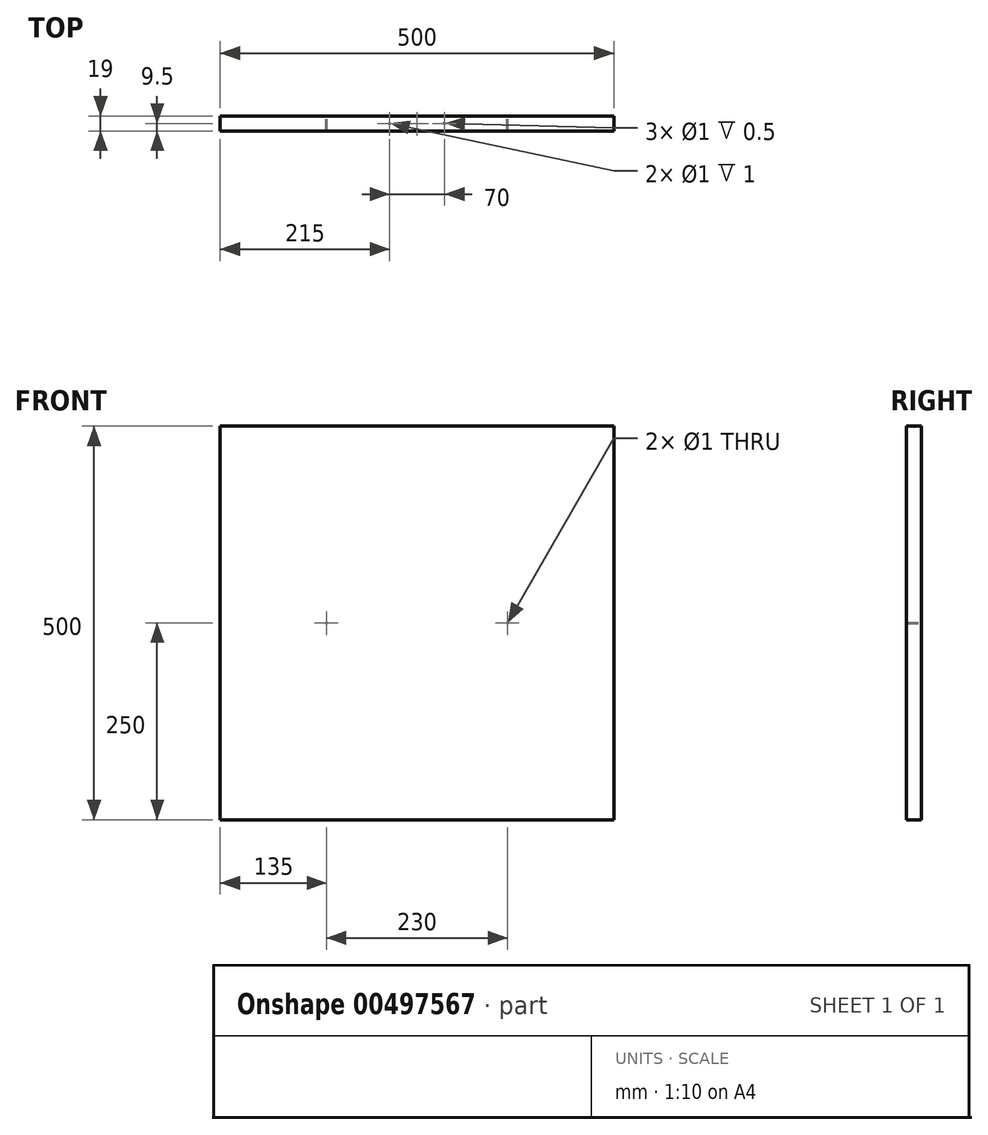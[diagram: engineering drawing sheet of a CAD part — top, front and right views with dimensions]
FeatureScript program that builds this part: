
annotation { "Feature Type Name" : "Feature", "Feature Type Description" : "" }
export const myFeature = defineFeature(function(context is Context, id is Id, definition is map)
    precondition{}
    {
        {
            var Q0;
            Q0=qCreatedBy(makeId("Front.planeOp"),FACE);
            var sketch = newSketch(context, id + "F0", { "sketchPlane" : qUnion([Q0])});
            skLineSegment(sketch, "E0.bottom", {"start": v(0, 500) * mm, "end": v(500, 500) * mm});
            skLineSegment(sketch, "E0.top", {"start": v(0, 0) * mm, "end": v(500, 0) * mm});
            skLineSegment(sketch, "E0.left", {"start": v(0, 500) * mm, "end": v(0, 0) * mm});
            skLineSegment(sketch, "E0.right", {"start": v(500, 500) * mm, "end": v(500, 0) * mm});
            skCircle(sketch, "E1", {"center": v(135, 250) * mm, "radius": 0.5 * mm});
            skLineSegment(sketch, "E2", {"start": v(250, 500) * mm, "end": v(250, 0) * mm, "construction": true});
            skCircle(sketch, "E3.MirrorC", {"center": v(365, 250) * mm, "radius": 0.5 * mm});
            skSolve(sketch);
        }
        {
            var Q0;
            Q0=makeQuery(id+"F0.imprint","IMPRINT",FACE,{"disambiguationData":[TD([[makeQuery(id+"F0.imprint","IMPRINT",EDGE,{"derivedFrom":sQuery(id+"F0.wireOp",EDGE,"E0.bottom")}),-1.0]])]});
            extrude(context, id + "F1", {"entities" : qUnion([Q0]), "depth" : 19 * mm});
        }
        {
            var Q0;
            Q0=makeQuery(id+"F1.opExtrude","SWEPT_FACE",FACE,{"disambiguationData":[OSD([sQuery(id+"F0.wireOp",EDGE,"E0.top")])]});
            var sketch = newSketch(context, id + "F2", { "sketchPlane" : qUnion([Q0])});
            skCircle(sketch, "E4", {"center": v(250, 9.5) * mm, "radius": 0.5 * mm});
            skPoint(sketch, "E4.centerSnap0", {"position": v(250, 0) * mm});
            skPoint(sketch, "E4.centerSnap1", {"position": v(0, 9.5) * mm});
            skLineSegment(sketch, "E5", {"start": v(250, 0) * mm, "end": v(250, 19) * mm, "construction": true});
            skCircle(sketch, "E6", {"center": v(215, 9.5) * mm, "radius": 0.5 * mm});
            skCircle(sketch, "E7.MirrorC", {"center": v(285, 9.5) * mm, "radius": 0.5 * mm});
            skSolve(sketch);
        }
        {
            var Q0;
            Q0 = qSketchRegion(id + "F2", true);
            extrude(context, id + "F3", {"entities" : qUnion([Q0]), "operationType" : NewBodyOperationType.REMOVE, "oppositeDirection" : true, "depth" : 1 * mm, "symmetric" : true});
        }
        {
            var Q0;
            Q0=makeQuery(id+"F1.opExtrude","SWEPT_FACE",FACE,{"disambiguationData":[OSD([sQuery(id+"F0.wireOp",EDGE,"E0.bottom")])]});
            var sketch = newSketch(context, id + "F4", { "sketchPlane" : qUnion([Q0])});
            skLineSegment(sketch, "E8", {"start": v(250, 0) * mm, "end": v(250, -19) * mm, "construction": true});
            skCircle(sketch, "E9", {"center": v(215, -9.5) * mm, "radius": 0.5 * mm});
            skPoint(sketch, "E9.centerSnap0", {"position": v(250, -9.5) * mm});
            skCircle(sketch, "E10.MirrorC", {"center": v(285, -9.5) * mm, "radius": 0.5 * mm});
            skSolve(sketch);
        }
        {
            var Q0;
            Q0 = qSketchRegion(id + "F4", true);
            extrude(context, id + "F5", {"entities" : qUnion([Q0]), "operationType" : NewBodyOperationType.REMOVE, "oppositeDirection" : true, "depth" : 1 * mm});
        }
    });
